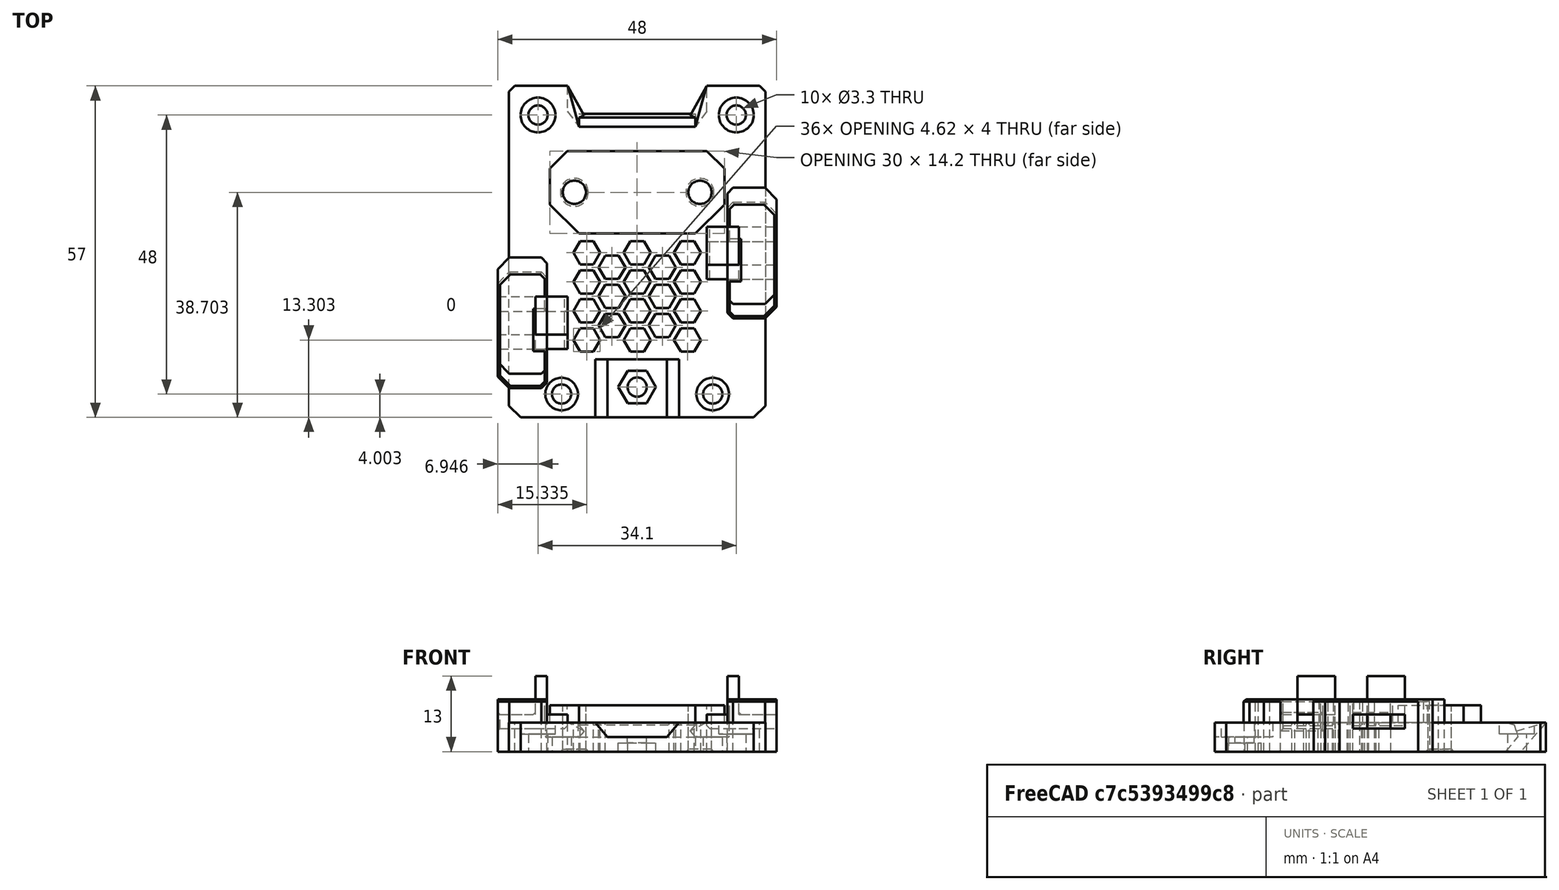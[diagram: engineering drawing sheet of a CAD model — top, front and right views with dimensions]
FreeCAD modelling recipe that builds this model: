
FCSTD DOCUMENT  (FreeCAD 0.19R24291 (Git))
Label: front-plate-light
License: Other
LicenseURL: GPL3
objects: Part::MultiFuse×10, Part::Feature×9, Part::Box×9, Part::Cut×8, Part::Cylinder×6, Part::Chamfer×4, Part::Extrusion×1, Part::MultiCommon×1
note: 48 computed .brp shape members not serialized (recipe doc carries the construction recipe); baked Part::Feature solids carry a one-line shape summary decoded from their .brp

FEATURE [Part::Feature] Part__Feature074_cs001
  shape: bbox 30 x 14.2 x 3e-07 mm, 0 faces, 0 solids (baked)
FEATURE [Part::Box] Box006  label="Cube006"
  AttacherType = Attacher::AttachEngine3D
  Height = 10
  Length = 15
  Placement = pos=(-7.5,-21,2.5) rot=(0,0,1;0rad)
  Width = 11
FEATURE [Part::Feature] Body007  label="Body002"
  Placement = pos=(26,0,0) rot=(0,0,1;0rad)
  shape: bbox 5.6 x 5.6 x 10 mm, 3 faces (baked)
FEATURE [Part::Extrusion] Extrude
  Base = -> Part__Feature074_cs001
  Dir = (0,0,1)
  DirMode = 2
  FaceMakerClass = Part::FaceMakerBullseye
  LengthFwd = 3
  LengthRev = 0
  Placement = pos=(0,0,-1) rot=(0,0,1;0rad)
  Solid = true
  Symmetric = false
FEATURE [Part::Feature] Body005  label="base-plate"
  shape: bbox 44.1 x 57 x 5 mm, 134 faces (baked)
FEATURE [Part::Feature] Body006  label="Body001"
  shape: bbox 5.6 x 5.6 x 10 mm, 3 faces (baked)
FEATURE [Part::MultiFuse] Fusion001007011043
  Shapes = -> [Extrude,Body005]
FEATURE [Part::Cylinder] Cylinder018
  Angle = 360
  AttacherType = Attacher::AttachEngine3D
  Height = 10
  Placement = pos=(-17.05,31,3.5) rot=(0,0,1;1.5708rad)
  Radius = 3
FEATURE [Part::Box] Box034  label="Cube030"
  AttacherType = Attacher::AttachEngine3D
  Height = 2.4
  Length = 12
  Placement = pos=(-24,-6.75,4.5) rot=(0,0,1;0rad)
  Width = 6.5
FEATURE [Part::Box] Box020  label="Cube018"
  AttacherType = Attacher::AttachEngine3D
  Height = 9
  Length = 8.5
  Placement = pos=(15.5,-1.5,0.5) rot=(0,0,1;0rad)
  Width = 20
FEATURE [Part::Feature] Part__Feature076  label="universal_face002"
  Placement = pos=(-0.00422634,7.50353,0.50127) rot=(-1,0,0;1.5708rad)
  shape: bbox 44.11 x 57.01 x 8.01 mm, 258 faces (baked)
FEATURE [Part::Cylinder] Cylinder017
  Angle = 360
  AttacherType = Attacher::AttachEngine3D
  Height = 10
  Placement = pos=(17.05,31,3.5) rot=(0,0,1;1.5708rad)
  Radius = 3
FEATURE [Part::MultiFuse] Fusion001007011011
  Shapes = -> [Cylinder018,Cylinder017]
FEATURE [Part::Box] Box021  label="Cube019"
  AttacherType = Attacher::AttachEngine3D
  Height = 9
  Length = 8.5
  Placement = pos=(-24,-13.5,0.5) rot=(0,0,1;0rad)
  Width = 20
FEATURE [Part::Cylinder] Cylinder
  Angle = 360
  AttacherType = Attacher::AttachEngine3D
  Height = 10
  Placement = pos=(-10.8,17.71,0) rot=(0,0,1;1.5708rad)
  Radius = 2
FEATURE [Part::Cylinder] Cylinder010
  Angle = 360
  AttacherType = Attacher::AttachEngine3D
  Height = 1
  Placement = pos=(0,-15.8,2) rot=(0,0,1;0rad)
  Radius = 1.65
FEATURE [Part::Box] Box007  label="Cube007"
  AttacherType = Attacher::AttachEngine3D
  Height = 2.4
  Length = 12
  Placement = pos=(12,5.25,4.5) rot=(0,0,1;0rad)
  Width = 6.5
FEATURE [Part::Cylinder] Cylinder001
  Angle = 360
  AttacherType = Attacher::AttachEngine3D
  Height = 10
  Placement = pos=(10.8,17.705,0) rot=(0,0,1;0rad)
  Radius = 2
FEATURE [Part::MultiFuse] Fusion002
  Shapes = -> [Cylinder001,Cylinder]
FEATURE [Part::Cut] Cut002
  Base = -> Fusion001007011043
  Placement = pos=(0,0,0.5) rot=(0,0,1;0rad)
  Tool = -> Fusion002
FEATURE [Part::Cut] Cut008004003012001003001010001005
  Base = -> Cut002
  Tool = -> Fusion001007011011
FEATURE [Part::MultiFuse] Fusion015
  Placement = pos=(0,0,3) rot=(0,0,1;0rad)
  Shapes = -> [Body007,Body006]
FEATURE [Part::Cut] Cut008004003012001003001010001006
  Base = -> Cut008004003012001003001010001005
  Tool = -> Fusion015
FEATURE [Part::Box] Box014  label="Cube012"
  AttacherType = Attacher::AttachEngine3D
  Height = 10
  Length = 26
  Placement = pos=(-13,27,0) rot=(0,0,1;0rad)
  Width = 10
FEATURE [Part::MultiCommon] Common001
  Placement = pos=(0,0,-0.00126953) rot=(0,0,1;0rad)
  Shapes = -> [Part__Feature076,Box014]
FEATURE [Part::Feature] Part__Feature075  label="universal_face001"
  Placement = pos=(-0.00422634,7.50353,0.50127) rot=(-1,0,0;1.5708rad)
  shape: bbox 44.11 x 57.01 x 8.01 mm, 258 faces (baked)
FEATURE [Part::Cut] Cut006
  Base = -> Box006
  Tool = -> Part__Feature075
FEATURE [Part::Cut] Cut008004003012001003001010001007
  Base = -> Cut008004003012001003001010001006
  Tool = -> Cut006
FEATURE [Part::Box] Box018  label="Cube016"
  AttacherType = Attacher::AttachEngine3D
  Height = 10
  Length = 26
  Placement = pos=(-13,27,0) rot=(0,0,1;0rad)
  Width = 10
FEATURE [Part::Cylinder] Cylinder009
  Angle = 360
  AttacherType = Attacher::AttachEngine3D
  Height = 1
  Placement = pos=(0,-15.8,2) rot=(0,0,1;0rad)
  Radius = 4
FEATURE [Part::Cut] Cut008004003010
  Base = -> Cylinder009
  Tool = -> Cylinder010
FEATURE [Part::MultiFuse] Fusion001007011025
  Shapes = -> [Cut008004003010,Cut008004003012001003001010001007]
FEATURE [Part::Cut] Cut008004003012001003001010001008
  Base = -> Fusion001007011025
  Tool = -> Box018
FEATURE [Part::MultiFuse] Fusion001007011026  label="face-plate-eva-base"
  Shapes = -> [Common001,Cut008004003012001003001010001008]
FEATURE [Part::MultiFuse] Fusion001007011026003
  Shapes = -> [Box021,Box020]
FEATURE [Part::Chamfer] Chamfer005021077002006007019003032007003
  Base = -> Fusion001007011026003
  Edges = 4 edges r=2: [Edge1,Edge3,Edge17,Edge19]
FEATURE [Part::Chamfer] Chamfer005021077002006007019003032007004  label="belt-block"
  Base = -> Chamfer005021077002006007019003032007003
  Edges = 4 edges r=1: [Edge17,Edge18,Edge35,Edge36]
FEATURE [Part::Box] Box037  label="Cube033"
  AttacherType = Attacher::AttachEngine3D
  Height = 9
  Length = 2
  Placement = pos=(15.5,5.25,4.5) rot=(0,0,1;0rad)
  Width = 6.5
FEATURE [Part::Box] Box038  label="Cube034"
  AttacherType = Attacher::AttachEngine3D
  Height = 9
  Length = 2
  Placement = pos=(-17.5,-6.75,4.5) rot=(0,0,1;0rad)
  Width = 6.5
FEATURE [Part::MultiFuse] Fusion001007011026006
  Shapes = -> [Box034,Box007]
FEATURE [Part::Chamfer] Chamfer005021077002006007019003032007004002
  Base = -> Fusion001007011026006
  Edges = 2 edges r=0.5: [Edge8,Edge16]
FEATURE [Part::MultiFuse] Fusion001007011026007  label="belt-cut"
  Shapes = -> [Chamfer005021077002006007019003032007004002,Box038,Box037]
FEATURE [Part::Feature] Chamfer005021077002006007019003032007004004  label="belt-block002"
  Placement = pos=(0,-2.5,0) rot=(0,0,1;0rad)
  shape: bbox 48 x 32 x 9 mm, 20 faces, 2 solids (baked)
FEATURE [Part::Feature] Fusion001007011026007002  label="belt-cut002"
  Placement = pos=(0,-2.5,0) rot=(0,0,1;0rad)
  shape: bbox 48 x 18.5 x 9 mm, 38 faces, 2 solids (baked)
FEATURE [Part::Feature] Fusion001007011026007003  label="face-plate-eva-base002"
  shape: bbox 44.1 x 57 x 8 mm, 175 faces (baked)
FEATURE [Part::MultiFuse] Fusion
  Shapes = -> [Fusion001007011026007003,Chamfer005021077002006007019003032007004004]
FEATURE [Part::Cut] Cut
  Base = -> Fusion
  Tool = -> Fusion001007011026007002
FEATURE [Part::Chamfer] Chamfer  label="common-front-plate-r1"
  Base = -> Cut
  Edges = 36 edges r=0.4: [Edge203,Edge206,Edge208,Edge209,Edge211,Edge221,Edge222,Edge225,Edge227,Edge231,Edge256,Edge258,Edge260,Edge262,Edge263,Edge274,Edge277,Edge278,Edge281,Edge284,Edge558,Edge560,Edge564,Edge565,Edge566,Edge567,Edge568,Edge569,Edge570,Edge571,Edge590,Edge591,Edge592,Edge593,Edge632,Edge650]
